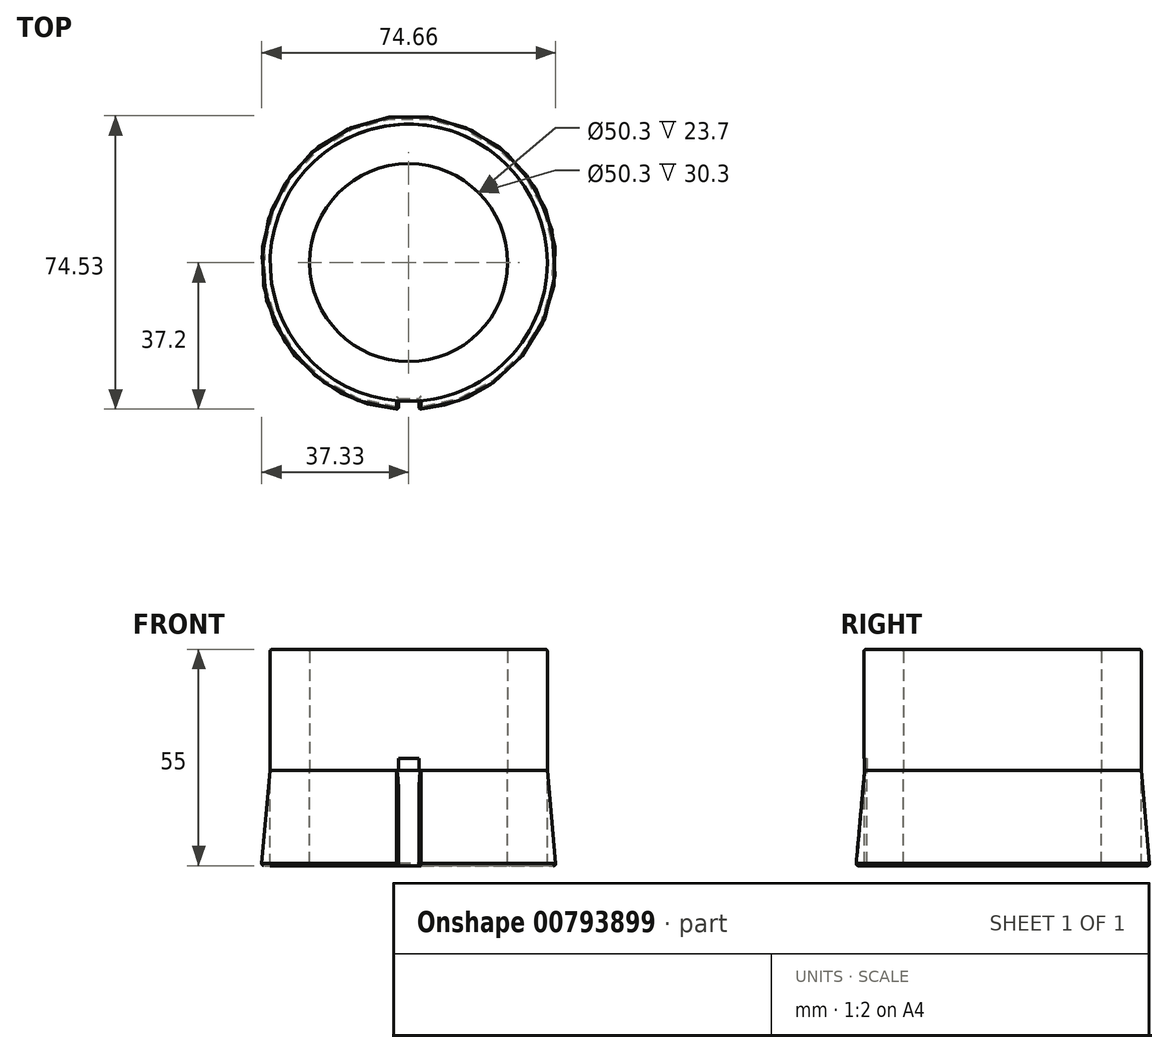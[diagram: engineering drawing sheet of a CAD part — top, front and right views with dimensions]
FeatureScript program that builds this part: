
annotation { "Feature Type Name" : "Feature", "Feature Type Description" : "" }
export const myFeature = defineFeature(function(context is Context, id is Id, definition is map)
    precondition{}
    {
        {
            var Q0;
            Q0=qCreatedBy(makeId("Top.planeOp"),FACE);
            var sketch = newSketch(context, id + "F0", { "sketchPlane" : qUnion([Q0])});
            skCircle(sketch, "E0", {"center": v(0, 0) * mm, "radius": 25.15 * mm});
            skCircle(sketch, "E1", {"center": v(0, 0) * mm, "radius": 37.38 * mm});
            skCircle(sketch, "E2", {"center": v(0, 0) * mm, "radius": 35.2 * mm});
            skLineSegment(sketch, "E3", {"start": v(0, 0) * mm, "end": v(0, -59.24) * mm});
            skLineSegment(sketch, "E4", {"start": v(0, -59.24) * mm, "end": v(2.6, -59.24) * mm});
            skLineSegment(sketch, "E5", {"start": v(0, -59.24) * mm, "end": v(-2.6, -59.24) * mm});
            skLineSegment(sketch, "E6.bottom", {"start": v(-2.6, -59.24) * mm, "end": v(2.6, -59.24) * mm});
            skLineSegment(sketch, "E6.top", {"start": v(-2.6, -34.48) * mm, "end": v(2.6, -34.48) * mm});
            skLineSegment(sketch, "E6.left", {"start": v(-2.6, -59.24) * mm, "end": v(-2.6, -34.48) * mm});
            skLineSegment(sketch, "E6.right", {"start": v(2.6, -59.24) * mm, "end": v(2.6, -34.48) * mm});
            skSolve(sketch);
        }
        {
            var Q0;
            Q0=makeQuery(id+"F0.imprint","IMPRINT",FACE,{"disambiguationData":[TD([[makeQuery(id+"F0.imprint","IMPRINT",EDGE,{"derivedFrom":sQuery(id+"F0.wireOp",EDGE,"E0")}),-1.0]])]});
            var Q1;
            {var subQ0=sQuery(id+"F0.wireOp",EDGE,"E3");var subQ1=sQuery(id+"F0.wireOp",EDGE,"E2");var subQ2=makeQuery(id+"F0.imprint","INTERSECT",VERTEX,{"derivedFrom":[subQ1,subQ0]});Q1=makeQuery(id+"F0.imprint","IMPRINT",FACE,{"disambiguationData":[TD([[makeQuery(id+"F0.imprint","IMPRINT",EDGE,{"disambiguationData":[TD([[subQ2,-1.0]])],"derivedFrom":subQ1}),1.0]])]});}
            var Q2;
            {var subQ0=sQuery(id+"F0.wireOp",EDGE,"E3");var subQ1=sQuery(id+"F0.wireOp",EDGE,"E2");var subQ2=makeQuery(id+"F0.imprint","INTERSECT",VERTEX,{"derivedFrom":[subQ1,subQ0]});Q2=makeQuery(id+"F0.imprint","IMPRINT",FACE,{"disambiguationData":[TD([[makeQuery(id+"F0.imprint","IMPRINT",EDGE,{"disambiguationData":[TD([[subQ2,1.0]])],"derivedFrom":subQ1}),1.0]])]});}
            extrude(context, id + "F1", {"entities" : qUnion([Q0, Q1, Q2]), "depth" : 30.8 * mm, "offsetDistance" : 25 * mm});
        }
        {
            var Q0;
            {var subQ0=sQuery(id+"F0.wireOp",EDGE,"E6.left");var subQ1=sQuery(id+"F0.wireOp",EDGE,"E1");var subQ2=makeQuery(id+"F0.imprint","INTERSECT",VERTEX,{"derivedFrom":[subQ1,subQ0]});Q0=makeQuery(id+"F0.imprint","IMPRINT",FACE,{"disambiguationData":[TD([[makeQuery(id+"F0.imprint","IMPRINT",EDGE,{"disambiguationData":[TD([[subQ2,1.0]])],"derivedFrom":subQ1}),1.0]])]});}
            extrude(context, id + "F2", {"entities" : qUnion([Q0]), "operationType" : NewBodyOperationType.ADD, "oppositeDirection" : true, "depth" : 24.2 * mm, "offsetDistance" : 25 * mm});
        }
        {
            var Q0;
            Q0=makeQuery(id+"F2.opExtrude","SWEPT_FACE",FACE,{"disambiguationData":[OSD([sQuery(id+"F0.wireOp",EDGE,"E6.right")])]});
            var sketch = newSketch(context, id + "F3", { "sketchPlane" : qUnion([Q0])});
            skLineSegment(sketch, "E7", {"start": v(35.1, 0) * mm, "end": v(37.28, -24.2) * mm});
            skLineSegment(sketch, "E8", {"start": v(37.28, -24.2) * mm, "end": v(37.28, 0) * mm});
            skLineSegment(sketch, "E9", {"start": v(37.28, 0) * mm, "end": v(35.1, 0) * mm});
            skSolve(sketch);
        }
        {
            var Q0;
            Q0=qCreatedBy(makeId("Front.planeOp"),FACE);
            var sketch = newSketch(context, id + "F4", { "sketchPlane" : qUnion([Q0])});
            skLineSegment(sketch, "E10", {"start": v(0, 0) * mm, "end": v(0, -85.8) * mm});
            skSolve(sketch);
        }
        {
            var Q0;
            Q0=makeQuery(id+"F3.imprint","IMPRINT",FACE,{"disambiguationData":[TD([[makeQuery(id+"F3.imprint","IMPRINT",EDGE,{"derivedFrom":sQuery(id+"F3.wireOp",EDGE,"E7")}),1.0]])]});
            var Q1;
            Q1=sQuery(id+"F4.wireOp",EDGE,"E10");
            revolve(context, id + "F5", {"operationType" : NewBodyOperationType.REMOVE, "surfaceOperationType" : NewSurfaceOperationType.NEW, "entities" : qUnion([Q0]), "axis" : qUnion([Q1]), "revolveType" : RevolveType.FULL, "oppositeDirection" : true});
        }
        {
            var Q0;
            Q0=makeQuery(id+"F0.imprint","IMPRINT",FACE,{"disambiguationData":[TD([[makeQuery(id+"F0.imprint","IMPRINT",EDGE,{"derivedFrom":sQuery(id+"F0.wireOp",EDGE,"E0")}),-1.0]])]});
            extrude(context, id + "F6", {"entities" : qUnion([Q0]), "oppositeDirection" : true, "depth" : 24.2 * mm, "offsetDistance" : 25 * mm});
        }
        {
            var Q0;
            {var subQ0=sQuery(id+"F0.wireOp",EDGE,"E3");var subQ1=sQuery(id+"F0.wireOp",EDGE,"E2");var subQ2=makeQuery(id+"F0.imprint","INTERSECT",VERTEX,{"derivedFrom":[subQ1,subQ0]});Q0=makeQuery(id+"F0.imprint","IMPRINT",FACE,{"disambiguationData":[TD([[makeQuery(id+"F0.imprint","IMPRINT",EDGE,{"disambiguationData":[TD([[subQ2,1.0]])],"derivedFrom":subQ1}),1.0]])]});}
            var Q1;
            {var subQ0=sQuery(id+"F0.wireOp",EDGE,"E3");var subQ1=sQuery(id+"F0.wireOp",EDGE,"E2");var subQ2=makeQuery(id+"F0.imprint","INTERSECT",VERTEX,{"derivedFrom":[subQ1,subQ0]});Q1=makeQuery(id+"F0.imprint","IMPRINT",FACE,{"disambiguationData":[TD([[makeQuery(id+"F0.imprint","IMPRINT",EDGE,{"disambiguationData":[TD([[subQ2,-1.0]])],"derivedFrom":subQ1}),1.0]])]});}
            extrude(context, id + "F7", {"entities" : qUnion([Q0, Q1]), "operationType" : NewBodyOperationType.REMOVE, "depth" : 3 * mm, "offsetDistance" : 25 * mm});
        }
        {
            var Q0;
            Q0=makeQuery(id+"F5.boolean.opBoolean","INTERSECT",EDGE,{"derivedFrom":[makeQuery(id+"F2.opExtrude","SWEPT_FACE",FACE,{"disambiguationData":[OSD([sQuery(id+"F0.wireOp",EDGE,"E6.right")])]}),makeQuery(id+"F5.opRevolve","SWEPT_FACE",FACE,{"disambiguationData":[OSD([sQuery(id+"F3.wireOp",EDGE,"E7")])]})]});
            var Q1;
            Q1=makeQuery(id+"F7.boolean.opBoolean","COPY",EDGE,{"derivedFrom":makeQuery(id+"F7.opExtrude","SWEPT_EDGE",EDGE,{"disambiguationData":[OSD([sQuery(id+"F0.wireOp",EDGE,"E2"),sQuery(id+"F0.wireOp",EDGE,"E6.right")])]})});
            var Q2;
            Q2=makeQuery(id+"F7.boolean.opBoolean","COPY",EDGE,{"derivedFrom":makeQuery(id+"F7.opExtrude","SWEPT_EDGE",EDGE,{"disambiguationData":[OSD([sQuery(id+"F0.wireOp",EDGE,"E2"),sQuery(id+"F0.wireOp",EDGE,"E6.left")])]})});
            var Q3;
            Q3=makeQuery(id+"F5.boolean.opBoolean","INTERSECT",EDGE,{"derivedFrom":[makeQuery(id+"F2.opExtrude","SWEPT_FACE",FACE,{"disambiguationData":[OSD([sQuery(id+"F0.wireOp",EDGE,"E6.left")])]}),makeQuery(id+"F5.opRevolve","SWEPT_FACE",FACE,{"disambiguationData":[OSD([sQuery(id+"F3.wireOp",EDGE,"E7")])]})]});
            var Q4;
            Q4=makeQuery(id+"F5.boolean.opBoolean","MERGE",EDGE,{"derivedFrom":[makeQuery(id+"F2.opExtrude","CAP_EDGE",EDGE,{"disambiguationData":[OSD([sQuery(id+"F0.wireOp",EDGE,"E1")])],"isStart":false}),makeQuery(id+"F5.opRevolve","SWEPT_EDGE",EDGE,{"disambiguationData":[OSD([sQuery(id+"F0.wireOp",EDGE,"E6.right"),sQuery(id+"F3.wireOp",EDGE,"E7"),sQuery(id+"F3.wireOp",EDGE,"E8")])]})]});
            var Q5;
            Q5=makeQuery(id+"F6.opExtrude","CAP_EDGE",EDGE,{"disambiguationData":[OSD([sQuery(id+"F0.wireOp",EDGE,"E0")])],"isStart":false});
            var Q6;
            Q6=makeQuery(id+"F1.opExtrude","CAP_EDGE",EDGE,{"disambiguationData":[OSD([sQuery(id+"F0.wireOp",EDGE,"E2")])],"isStart":false});
            var Q7;
            Q7=makeQuery(id+"F1.opExtrude","CAP_EDGE",EDGE,{"disambiguationData":[OSD([sQuery(id+"F0.wireOp",EDGE,"E0")])],"isStart":false});
            var Q8;
            Q8=makeQuery(id+"F2.opExtrude","CAP_EDGE",EDGE,{"disambiguationData":[OSD([sQuery(id+"F0.wireOp",EDGE,"E6.left")])],"isStart":false});
            var Q9;
            Q9=makeQuery(id+"F6.opExtrude","CAP_EDGE",EDGE,{"disambiguationData":[OSD([sQuery(id+"F0.wireOp",EDGE,"E6.left")])],"isStart":false});
            var Q10;
            Q10=makeQuery(id+"F6.opExtrude","CAP_EDGE",EDGE,{"disambiguationData":[OSD([sQuery(id+"F0.wireOp",EDGE,"E6.top")])],"isStart":false});
            var Q11;
            Q11=makeQuery(id+"F6.opExtrude","CAP_EDGE",EDGE,{"disambiguationData":[OSD([sQuery(id+"F0.wireOp",EDGE,"E6.right")])],"isStart":false});
            var Q12;
            Q12=makeQuery(id+"F2.opExtrude","CAP_EDGE",EDGE,{"disambiguationData":[OSD([sQuery(id+"F0.wireOp",EDGE,"E6.right")])],"isStart":false});
            var Q13;
            Q13=makeQuery(id+"F7.boolean.opBoolean","COPY",EDGE,{"derivedFrom":makeQuery(id+"F7.opExtrude","CAP_EDGE",EDGE,{"disambiguationData":[OSD([sQuery(id+"F0.wireOp",EDGE,"E2")])],"isStart":false})});
            fillet(context, id + "F8", {"entities" : qUnion([Q0, Q1, Q2, Q3, Q4, Q5, Q6, Q7, Q8, Q9, Q10, Q11, Q12, Q13]), "radius" : .5 * mm, "tangentPropagation" : true, "allowEdgeOverflow" : false});
        }
    });
